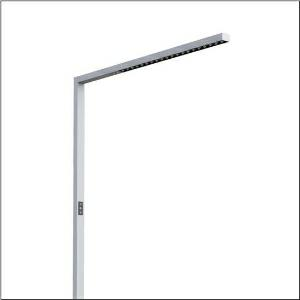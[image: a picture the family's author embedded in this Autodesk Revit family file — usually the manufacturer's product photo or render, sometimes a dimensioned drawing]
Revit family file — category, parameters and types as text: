
# Revit family: silica_r__31_floor_51my52fa4cs_7d3f
name_source: partatom
category: Lighting Fixtures
units: mm (PartAtom-declared; Revit-internal decimal feet)

## family parameters
Cut with Voids When Loaded = No
Host = Face
Light Source = No
Part Type = Normal
Room Calculation Point = No
Round Connector Dimension = Use Diameter
Shared = No

## types (1)
- Silica® 31 Floor (1 x LED, 10600 lm, 75 W, 4000K)
    Apparent Load = 75 VA
    CIE Flux Codes = 86 100 100 24 100
    Color Rendering = 80
    Color Temperature = 4000K
    Default Elevation = 1800 mm
    Description = Silica® 31 Floor, floorstanding luminaire, secondary optical cover: cover panel, of PMMA, light emission: direct/indirect distribution, primary light characteristic: symmetric, installation type: not mounted, LED, rated luminous flux: 10.600lm, luminous efficacy: 141lm/W, light colour: 840, colour temperature: 4000K, control gear: Touchdim, daylight-dependent control, with cable with plug, mains connection: 230V, AC, 50Hz, connection cable pre-assembled, rated input power: 75W, luminaire head, of aluminium, metallic grey (RAL 9006), length: 1.203mm, width: 52mm, supporting column, angular, of aluminium, metallic grey (RAL 9006), baseplate, of steel, metallic grey (RAL 9006), protection rating (complete): IP20, insulation class (complete): insulation class I (protective earthing), certification: CE, permissible operating ambient temperature: -20..+40°C, standard: EN 50419, packaging unit: 1 piece
    Height = 36 mm
    Lamp = 1 x LED
    Lamp Light Flux = 10600 lm
    Lamp Power = 75 W
    Lamp count = 1
    Length = 1203 mm
    Luminous efficacy = 141 lm/W
    Manufacturer = Siteco
    ModVariant = No
    Model = 51MY52FA4CS
    Mounting Place = Floor
    Mounting Type = Freestanding
    Number of Poles = 1
    OnlyDefault = Yes
    Power Factor = 1
    Product Name = Silica® 31 Floor
    Product group = floorstanding luminaire
    ProductGroupID = 1302
    Protection Class = Protection class I
    Protection Degree = IP 20
    RLX_Detail_Level = 1
    RLX_Emergency_Light_Flux = 0 lm
    RLX_Emergency_Type = 0
    RLX_Emergency_Type_DB = No
    RlxData = <blob elided: 19577 chars, md5=b0147355>
    Socket = socket
    Standby Power = 0 W
    System Light Flux = 10600 lm
    System Power = 75 W
    Type Comments = Product without accessories
    Type Image = l_1275303.jpg
    URL = http://relux.com
    VarID = ---
    Voltage = 0 V
    Weight = 0.00 kg
    Width = 52 mm  [stored 0.170604 ft]

note: [stored X ft] marks values corroborated as IEEE doubles in the binary element streams (Revit-internal decimal feet)

## geometry (parser evidence)
native form markers: Blend x4, Sweep x15
no freeform markers — native parametric forms only
